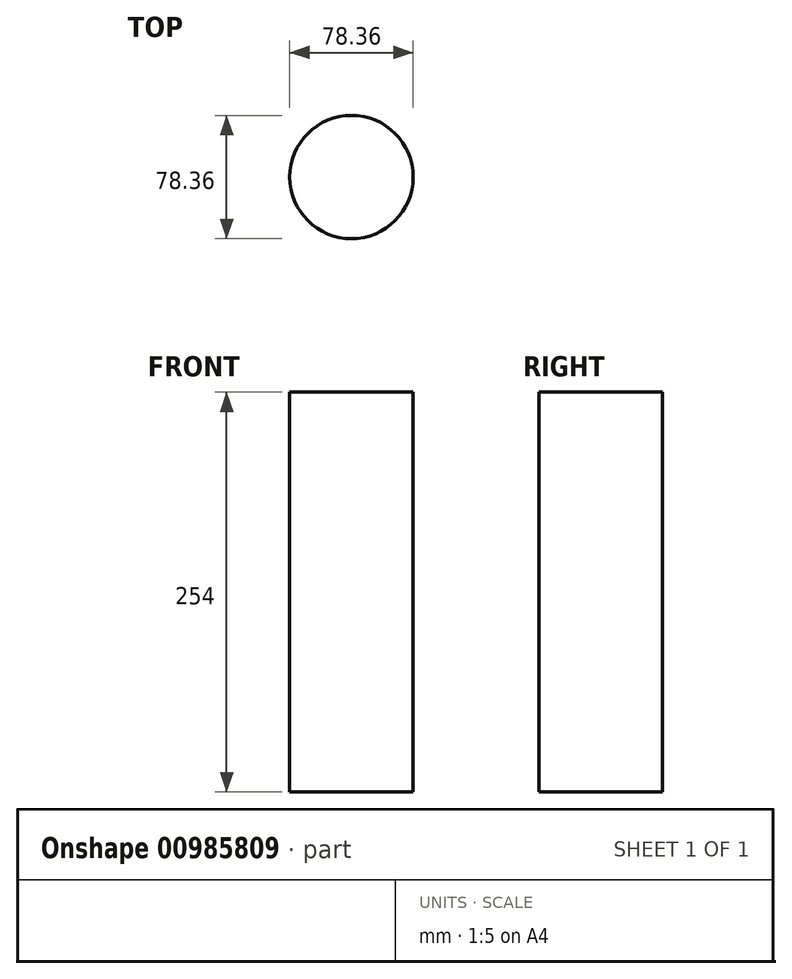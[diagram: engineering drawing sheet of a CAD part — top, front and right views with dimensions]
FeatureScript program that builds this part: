
annotation { "Feature Type Name" : "Feature", "Feature Type Description" : "" }
export const myFeature = defineFeature(function(context is Context, id is Id, definition is map)
    precondition{}
    {
        {
            var Q0;
            Q0=qCreatedBy(makeId("Top.planeOp"),FACE);
            var sketch = newSketch(context, id + "F0", { "sketchPlane" : qUnion([Q0])});
            skCircle(sketch, "E0", {"center": v(0, 0) * mm, "radius": 39.18 * mm});
            skSolve(sketch);
        }
        {
            var Q0;
            Q0 = qSketchRegion(id + "F0", true);
            extrude(context, id + "F1", {"entities" : qUnion([Q0]), "depth" : 254 * mm, "offsetDistance" : 25.4 * mm});
        }
    });
